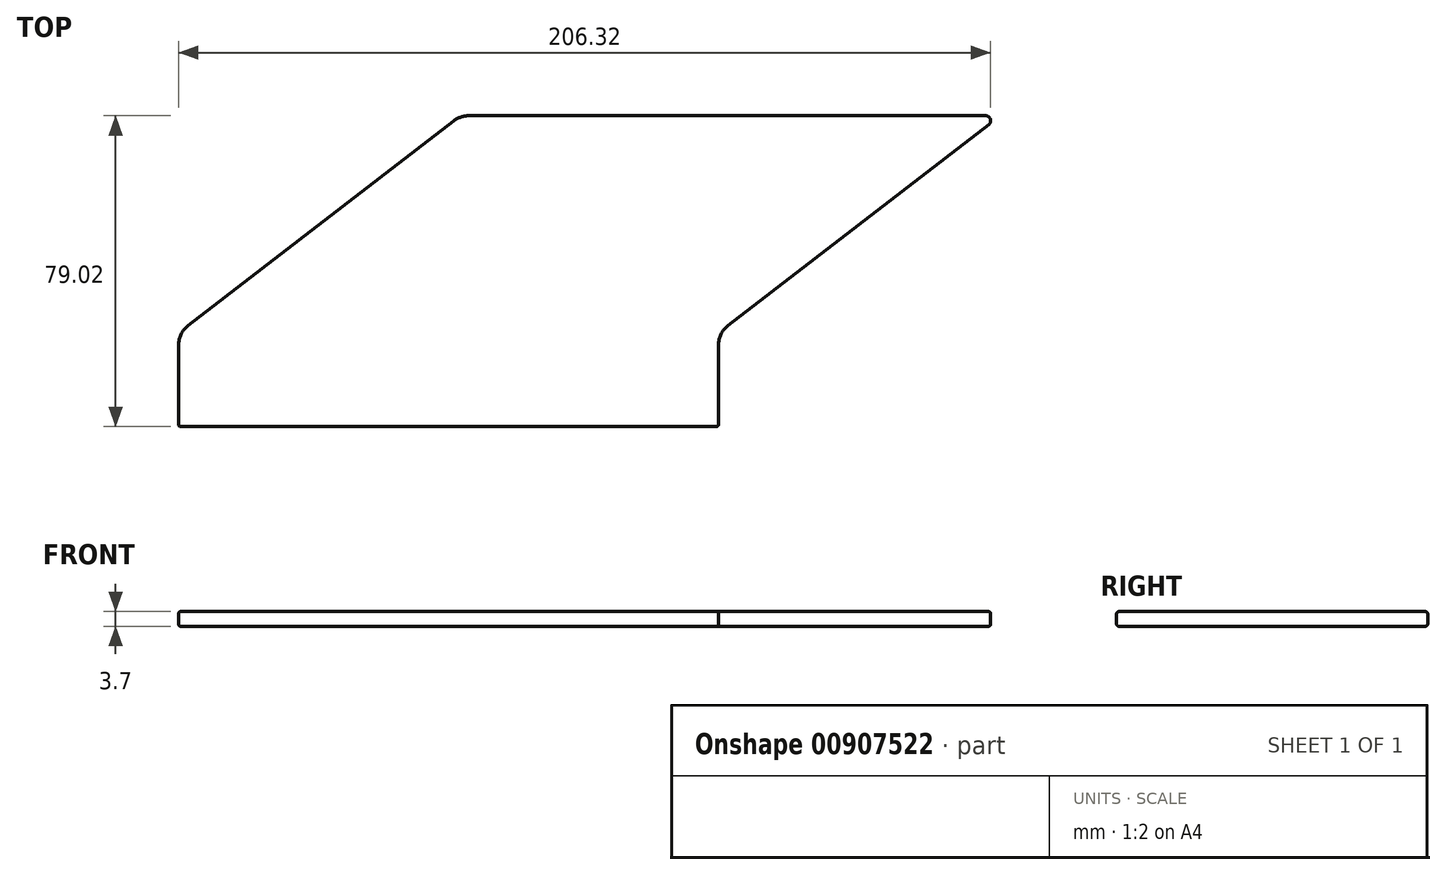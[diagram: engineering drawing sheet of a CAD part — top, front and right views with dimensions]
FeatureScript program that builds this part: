
annotation { "Feature Type Name" : "Feature", "Feature Type Description" : "" }
export const myFeature = defineFeature(function(context is Context, id is Id, definition is map)
    precondition{}
    {
        {
            var Q0;
            Q0=qCreatedBy(makeId("Top.planeOp"),FACE);
            var sketch = newSketch(context, id + "F0", { "sketchPlane" : qUnion([Q0])});
            skLineSegment(sketch, "E0", {"start": v(0, 0) * mm, "end": v(137.16, 0) * mm});
            skLineSegment(sketch, "E1", {"start": v(137.16, 0) * mm, "end": v(137.16, 20.69) * mm});
            skLineSegment(sketch, "E2", {"start": v(205.83, 76.74) * mm, "end": v(139.63, 25.72) * mm});
            skLineSegment(sketch, "E3", {"start": v(73.78, 79.02) * mm, "end": v(205.05, 79.02) * mm});
            skLineSegment(sketch, "E4", {"start": v(0, 0) * mm, "end": v(0, 20.69) * mm});
            skLineSegment(sketch, "E5", {"start": v(2.47, 25.72) * mm, "end": v(69.9, 77.7) * mm});
            skPoint(sketch, "E6.visualSharp", {"position": v(0, 23.81) * mm});
            skArc(sketch, "E6.filletArc", {"start": v(2.47, 25.72) * mm, "mid": v(0.65, 23.5) * mm, "end": v(0, 20.69) * mm});
            skPoint(sketch, "E7.visualSharp", {"position": v(90.53, 93.6) * mm});
            skArc(sketch, "E7.filletArc", {"start": v(73.78, 79.02) * mm, "mid": v(71.73, 78.68) * mm, "end": v(69.9, 77.7) * mm});
            skPoint(sketch, "E8.visualSharp", {"position": v(137.16, 23.81) * mm});
            skArc(sketch, "E8.filletArc", {"start": v(139.63, 25.72) * mm, "mid": v(137.81, 23.5) * mm, "end": v(137.16, 20.69) * mm});
            skPoint(sketch, "E9.visualSharp", {"position": v(227.69, 93.6) * mm});
            skArc(sketch, "E9.filletArc", {"start": v(205.83, 76.74) * mm, "mid": v(206.25, 78.16) * mm, "end": v(205.05, 79.02) * mm});
            skSolve(sketch);
        }
        {
            var Q0;
            Q0=makeQuery(id+"F0.imprint","IMPRINT",FACE,{"disambiguationData":[TD([[makeQuery(id+"F0.imprint","IMPRINT",EDGE,{"derivedFrom":sQuery(id+"F0.wireOp",EDGE,"E0")}),1.0]])]});
            extrude(context, id + "F1", {"entities" : qUnion([Q0]), "depth" : 3.7 * mm, "offsetDistance" : 25.4 * mm});
        }
        {
            var Q0;
            Q0=makeQuery(id+"F1.opExtrude","CAP_EDGE",EDGE,{"disambiguationData":[OSD([sQuery(id+"F0.wireOp",EDGE,"E0")])],"isStart":false});
            var Q1;
            Q1=makeQuery(id+"F1.opExtrude","CAP_EDGE",EDGE,{"disambiguationData":[OSD([sQuery(id+"F0.wireOp",EDGE,"E0")])],"isStart":true});
            var Q2;
            Q2=makeQuery(id+"F1.opExtrude","SWEPT_EDGE",EDGE,{"disambiguationData":[OSD([sQuery(id+"F0.wireOp",EDGE,"E0"),sQuery(id+"F0.wireOp",EDGE,"E4")])]});
            var Q3;
            Q3=makeQuery(id+"F1.opExtrude","CAP_EDGE",EDGE,{"disambiguationData":[OSD([sQuery(id+"F0.wireOp",EDGE,"E4")])],"isStart":false});
            var Q4;
            Q4=makeQuery(id+"F1.opExtrude","CAP_EDGE",EDGE,{"disambiguationData":[OSD([sQuery(id+"F0.wireOp",EDGE,"E1")])],"isStart":true});
            var Q5;
            Q5=makeQuery(id+"F1.opExtrude","SWEPT_EDGE",EDGE,{"disambiguationData":[OSD([sQuery(id+"F0.wireOp",EDGE,"E0"),sQuery(id+"F0.wireOp",EDGE,"E1")])]});
            fillet(context, id + "F2", {"entities" : qUnion([Q0, Q1, Q2, Q3, Q4, Q5]), "radius" : 0.5 * mm, "tangentPropagation" : true, "allowEdgeOverflow" : false});
        }
    });
